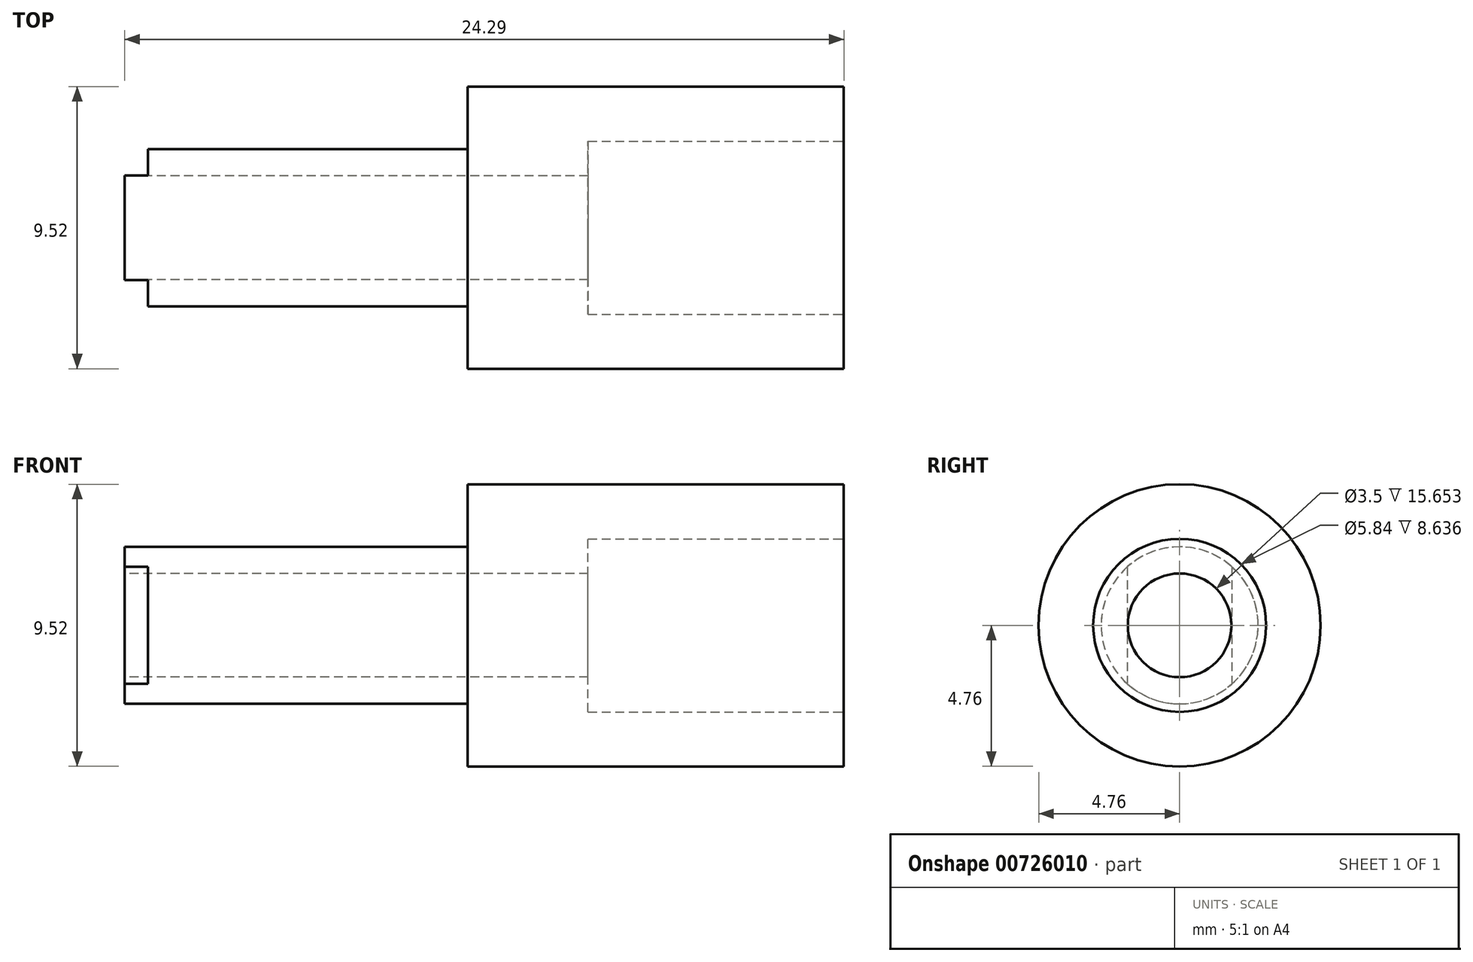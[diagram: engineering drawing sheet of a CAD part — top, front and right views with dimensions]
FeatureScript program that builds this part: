
annotation { "Feature Type Name" : "Feature", "Feature Type Description" : "" }
export const myFeature = defineFeature(function(context is Context, id is Id, definition is map)
    precondition{}
    {
        {
            var Q0;
            Q0=qCreatedBy(makeId("Right.planeOp"),FACE);
            var sketch = newSketch(context, id + "F0", { "sketchPlane" : qUnion([Q0])});
            skCircle(sketch, "E0", {"center": v(0, 0) * mm, "radius": 2.65 * mm});
            skCircle(sketch, "E1", {"center": v(0, 0) * mm, "radius": 1.75 * mm});
            skLineSegment(sketch, "E2.bottom", {"start": v(-1.77, 1.98) * mm, "end": v(1.77, 1.98) * mm});
            skLineSegment(sketch, "E2.top", {"start": v(-1.77, -1.98) * mm, "end": v(1.77, -1.98) * mm});
            skLineSegment(sketch, "E2.left", {"start": v(-1.77, 1.98) * mm, "end": v(-1.77, -1.98) * mm});
            skLineSegment(sketch, "E2.right", {"start": v(1.77, 1.98) * mm, "end": v(1.77, -1.98) * mm});
            skCircle(sketch, "E3", {"center": v(0, 0) * mm, "radius": 4.76 * mm});
            skCircle(sketch, "E4", {"center": v(0, 0) * mm, "radius": 3.97 * mm});
            skCircle(sketch, "E5", {"center": v(0, 0) * mm, "radius": 3.3 * mm, "construction": true});
            skLineSegment(sketch, "E6", {"start": v(-3.95, 0.4) * mm, "end": v(-3.28, 0.4) * mm});
            skLineSegment(sketch, "E7", {"start": v(-3.28, 0.4) * mm, "end": v(-2.65, 0.13) * mm});
            skLineSegment(sketch, "E8", {"start": v(1.75, 0) * mm, "end": v(-1.75, 0) * mm, "construction": true});
            skPoint(sketch, "E8.endSnap0", {"position": v(-1.77, 0) * mm});
            skLineSegment(sketch, "E9.MirrorCS", {"start": v(-3.95, -0.4) * mm, "end": v(-3.28, -0.4) * mm});
            skLineSegment(sketch, "E10.MirrorCS", {"start": v(-3.28, -0.4) * mm, "end": v(-2.65, -0.13) * mm});
            skLineSegment(sketch, "E11.1.0", {"start": v(1.62, -3.62) * mm, "end": v(1.29, -3.04) * mm});
            skLineSegment(sketch, "E11.1.1", {"start": v(1.29, -3.04) * mm, "end": v(1.21, -2.36) * mm});
            skLineSegment(sketch, "E11.1.2", {"start": v(2, -2.63) * mm, "end": v(1.43, -2.23) * mm});
            skLineSegment(sketch, "E11.1.3", {"start": v(2.33, -3.22) * mm, "end": v(2, -2.63) * mm});
            skLineSegment(sketch, "E11.2.0", {"start": v(2.33, 3.22) * mm, "end": v(2, 2.63) * mm});
            skLineSegment(sketch, "E11.2.1", {"start": v(2, 2.63) * mm, "end": v(1.43, 2.23) * mm});
            skLineSegment(sketch, "E11.2.2", {"start": v(1.29, 3.04) * mm, "end": v(1.21, 2.36) * mm});
            skLineSegment(sketch, "E11.2.3", {"start": v(1.62, 3.62) * mm, "end": v(1.29, 3.04) * mm});
            skSolve(sketch);
        }
        {
            var Q0;
            {var subQ0=sQuery(id+"F0.wireOp",EDGE,"E2.left");var subQ4=sQuery(id+"F0.wireOp",EDGE,"E1");var subQ5=makeQuery(id+"F0.imprint","INTERSECT",VERTEX,{"disambiguationData":[OD(0.0)],"derivedFrom":[subQ4,subQ0]});Q0=makeQuery(id+"F0.imprint","IMPRINT",FACE,{"disambiguationData":[TD([[makeQuery(id+"F0.imprint","IMPRINT",EDGE,{"disambiguationData":[TD([[subQ5,-1.0]])],"derivedFrom":subQ4}),-1.0]])]});}
            var Q1;
            {var subQ0=sQuery(id+"F0.wireOp",EDGE,"E2.bottom");Q1=makeQuery(id+"F0.imprint","IMPRINT",FACE,{"disambiguationData":[TD([[makeQuery(id+"F0.imprint","IMPRINT",EDGE,{"derivedFrom":subQ0}),1.0]])]});}
            var Q2;
            {var subQ5=sQuery(id+"F0.wireOp",EDGE,"E2.bottom");Q2=makeQuery(id+"F0.imprint","IMPRINT",FACE,{"disambiguationData":[TD([[makeQuery(id+"F0.imprint","IMPRINT",EDGE,{"derivedFrom":subQ5}),-1.0]])]});}
            var Q3;
            {var subQ0=sQuery(id+"F0.wireOp",EDGE,"E2.right");var subQ4=sQuery(id+"F0.wireOp",EDGE,"E1");var subQ5=makeQuery(id+"F0.imprint","INTERSECT",VERTEX,{"disambiguationData":[OD(0.0)],"derivedFrom":[subQ4,subQ0]});Q3=makeQuery(id+"F0.imprint","IMPRINT",FACE,{"disambiguationData":[TD([[makeQuery(id+"F0.imprint","IMPRINT",EDGE,{"disambiguationData":[TD([[subQ5,1.0]])],"derivedFrom":subQ4}),-1.0]])]});}
            var Q4;
            {var subQ0=sQuery(id+"F0.wireOp",EDGE,"E2.top");Q4=makeQuery(id+"F0.imprint","IMPRINT",FACE,{"disambiguationData":[TD([[makeQuery(id+"F0.imprint","IMPRINT",EDGE,{"derivedFrom":subQ0}),-1.0]])]});}
            var Q5;
            {var subQ5=sQuery(id+"F0.wireOp",EDGE,"E2.top");Q5=makeQuery(id+"F0.imprint","IMPRINT",FACE,{"disambiguationData":[TD([[makeQuery(id+"F0.imprint","IMPRINT",EDGE,{"derivedFrom":subQ5}),1.0]])]});}
            var Q6;
            {var subQ0=sQuery(id+"F0.wireOp",EDGE,"E2.left");Q6=makeQuery(id+"F0.imprint","IMPRINT",FACE,{"disambiguationData":[TD([[makeQuery(id+"F0.imprint","IMPRINT",EDGE,{"derivedFrom":subQ0}),-1.0]])]});}
            var Q7;
            {var subQ0=sQuery(id+"F0.wireOp",EDGE,"E2.right");Q7=makeQuery(id+"F0.imprint","IMPRINT",FACE,{"disambiguationData":[TD([[makeQuery(id+"F0.imprint","IMPRINT",EDGE,{"derivedFrom":subQ0}),1.0]])]});}
            extrude(context, id + "F1", {"entities" : qUnion([Q0, Q1, Q2, Q3, Q4, Q5, Q6, Q7]), "depth" : 10.8 * mm, "offsetDistance" : 25.4 * mm});
        }
        {
            var Q0;
            {var subQ5=sQuery(id+"F0.wireOp",EDGE,"E2.bottom");Q0=makeQuery(id+"F0.imprint","IMPRINT",FACE,{"disambiguationData":[TD([[makeQuery(id+"F0.imprint","IMPRINT",EDGE,{"derivedFrom":subQ5}),-1.0]])]});}
            var Q1;
            {var subQ5=sQuery(id+"F0.wireOp",EDGE,"E2.top");Q1=makeQuery(id+"F0.imprint","IMPRINT",FACE,{"disambiguationData":[TD([[makeQuery(id+"F0.imprint","IMPRINT",EDGE,{"derivedFrom":subQ5}),1.0]])]});}
            var Q2;
            {var subQ0=sQuery(id+"F0.wireOp",EDGE,"E2.bottom");Q2=makeQuery(id+"F0.imprint","IMPRINT",FACE,{"disambiguationData":[TD([[makeQuery(id+"F0.imprint","IMPRINT",EDGE,{"derivedFrom":subQ0}),1.0]])]});}
            var Q3;
            {var subQ0=sQuery(id+"F0.wireOp",EDGE,"E2.top");Q3=makeQuery(id+"F0.imprint","IMPRINT",FACE,{"disambiguationData":[TD([[makeQuery(id+"F0.imprint","IMPRINT",EDGE,{"derivedFrom":subQ0}),-1.0]])]});}
            extrude(context, id + "F2", {"entities" : qUnion([Q0, Q1, Q2, Q3]), "operationType" : NewBodyOperationType.ADD, "oppositeDirection" : true, "depth" : 0.8 * mm, "offsetDistance" : 25.4 * mm});
        }
        {
            var Q0;
            Q0=makeQuery(id+"F1.opExtrude","CAP_FACE",FACE,{"disambiguationData":[OSD([sQuery(id+"F0.wireOp",EDGE,"E0"),sQuery(id+"F0.wireOp",EDGE,"E1")])],"isStart":false});
            var sketch = newSketch(context, id + "F3", { "sketchPlane" : qUnion([Q0])});
            skCircle(sketch, "E12", {"center": v(0, 0) * mm, "radius": 4.76 * mm});
            skSolve(sketch);
        }
        {
            var Q0;
            Q0=makeQuery(id+"F3.imprint","IMPRINT",FACE,{"disambiguationData":[TD([[makeQuery(id+"F3.imprint","IMPRINT",EDGE,{"derivedFrom":sQuery(id+"F3.wireOp",EDGE,"E12")}),1.0]])]});
            var Q1;
            Q1=makeQuery(id+"F3.imprint","IMPRINT",FACE,{"disambiguationData":[TD([[makeQuery(id+"F3.imprint","IMPRINT",EDGE,{"derivedFrom":makeQuery(id+"F1.opExtrude","CAP_EDGE",EDGE,{"disambiguationData":[OSD([sQuery(id+"F0.wireOp",EDGE,"E0")])],"isStart":false})}),1.0]])]});
            extrude(context, id + "F4", {"entities" : qUnion([Q0, Q1]), "operationType" : NewBodyOperationType.ADD, "depth" : 12.7 * mm, "offsetDistance" : 25.4 * mm});
        }
        {
            var Q0;
            Q0=makeQuery(id+"F4.opExtrude","CAP_FACE",FACE,{"disambiguationData":[OSD([sQuery(id+"F0.wireOp",EDGE,"E1"),sQuery(id+"F3.wireOp",EDGE,"E12")])],"isStart":false});
            var sketch = newSketch(context, id + "F5", { "sketchPlane" : qUnion([Q0])});
            skCircle(sketch, "E13", {"center": v(0, 0) * mm, "radius": 2.92 * mm});
            skSolve(sketch);
        }
        {
            var Q0;
            Q0=makeQuery(id+"F5.imprint","IMPRINT",FACE,{"disambiguationData":[TD([[makeQuery(id+"F5.imprint","IMPRINT",EDGE,{"derivedFrom":sQuery(id+"F5.wireOp",EDGE,"E13")}),1.0]])]});
            extrude(context, id + "F6", {"entities" : qUnion([Q0]), "operationType" : NewBodyOperationType.REMOVE, "oppositeDirection" : true, "depth" : 8.64 * mm, "offsetDistance" : 25.4 * mm});
        }
    });
